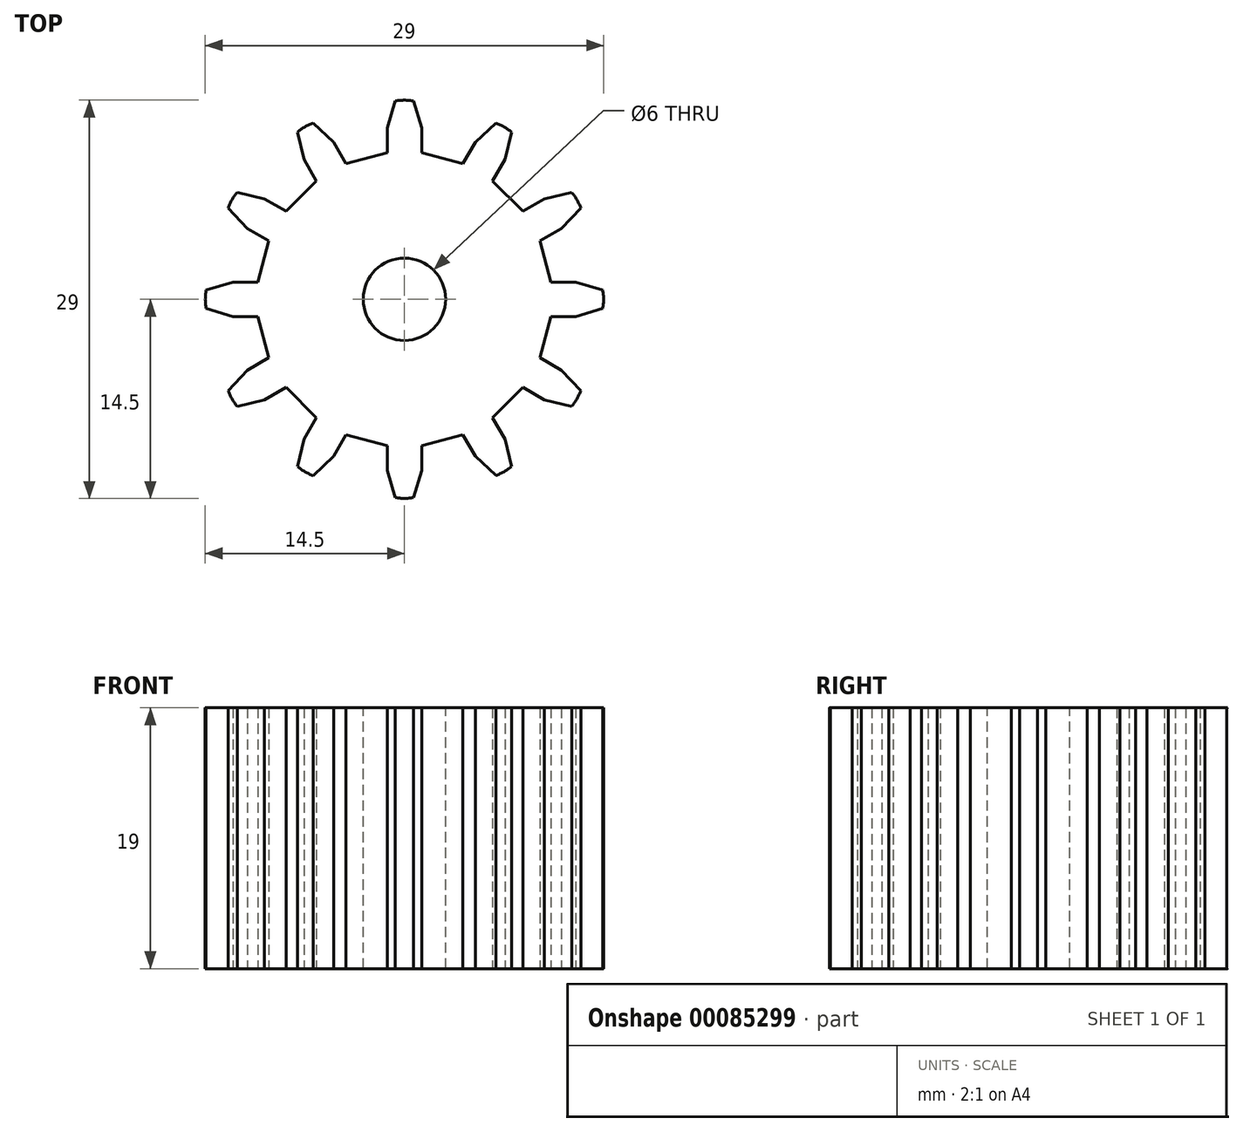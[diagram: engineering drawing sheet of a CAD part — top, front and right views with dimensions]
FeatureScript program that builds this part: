
annotation { "Feature Type Name" : "Feature", "Feature Type Description" : "" }
export const myFeature = defineFeature(function(context is Context, id is Id, definition is map)
    precondition{}
    {
        {
            var Q0;
            Q0=qCreatedBy(makeId("Top.planeOp"),FACE);
            var sketch = newSketch(context, id + "F0", { "sketchPlane" : qUnion([Q0])});
            skCircle(sketch, "E0", {"center": v(0, 0) * mm, "radius": 14.5 * mm});
            skArc(sketch, "E1", {"start": v(-1.25, 10.68) * mm, "mid": v(0, -10.75) * mm, "end": v(1.25, 10.68) * mm});
            skLineSegment(sketch, "E2", {"start": v(0, 10.75) * mm, "end": v(0, 14.5) * mm});
            skLineSegment(sketch, "E3.0", {"start": v(1.25, 10.68) * mm, "end": v(1.25, 14.29) * mm});
            skLineSegment(sketch, "E4.0", {"start": v(-1.25, 10.68) * mm, "end": v(-1.25, 14.29) * mm});
            skArc(sketch, "E5.trimOffspring", {"start": v(1.25, 14.29) * mm, "mid": v(0, 14.5) * mm, "end": v(-1.25, 14.29) * mm});
            skLineSegment(sketch, "E6", {"start": v(-1.25, 14.29) * mm, "end": v(-1.25, 14.45) * mm});
            skLineSegment(sketch, "E7.1.0", {"start": v(-4.26, 9.87) * mm, "end": v(-6.06, 13) * mm});
            skArc(sketch, "E7.1.1", {"start": v(-6.06, 13) * mm, "mid": v(-7.25, 12.56) * mm, "end": v(-8.23, 11.75) * mm});
            skLineSegment(sketch, "E7.1.2", {"start": v(-6.42, 8.62) * mm, "end": v(-8.23, 11.75) * mm});
            skLineSegment(sketch, "E7.2.0", {"start": v(-8.62, 6.42) * mm, "end": v(-11.75, 8.23) * mm});
            skArc(sketch, "E7.2.1", {"start": v(-11.75, 8.23) * mm, "mid": v(-12.56, 7.25) * mm, "end": v(-13, 6.06) * mm});
            skLineSegment(sketch, "E7.2.2", {"start": v(-9.87, 4.26) * mm, "end": v(-13, 6.06) * mm});
            skLineSegment(sketch, "E7.3.0", {"start": v(-10.68, 1.25) * mm, "end": v(-14.29, 1.25) * mm});
            skArc(sketch, "E7.3.1", {"start": v(-14.29, 1.25) * mm, "mid": v(-14.5, 0) * mm, "end": v(-14.29, -1.25) * mm});
            skLineSegment(sketch, "E7.3.2", {"start": v(-10.68, -1.25) * mm, "end": v(-14.29, -1.25) * mm});
            skLineSegment(sketch, "E7.4.0", {"start": v(-9.87, -4.26) * mm, "end": v(-13, -6.06) * mm});
            skArc(sketch, "E7.4.1", {"start": v(-13, -6.06) * mm, "mid": v(-12.56, -7.25) * mm, "end": v(-11.75, -8.23) * mm});
            skLineSegment(sketch, "E7.4.2", {"start": v(-8.62, -6.42) * mm, "end": v(-11.75, -8.23) * mm});
            skLineSegment(sketch, "E7.5.0", {"start": v(-6.42, -8.62) * mm, "end": v(-8.23, -11.75) * mm});
            skArc(sketch, "E7.5.1", {"start": v(-8.23, -11.75) * mm, "mid": v(-7.25, -12.56) * mm, "end": v(-6.06, -13) * mm});
            skLineSegment(sketch, "E7.5.2", {"start": v(-4.26, -9.87) * mm, "end": v(-6.06, -13) * mm});
            skLineSegment(sketch, "E7.6.0", {"start": v(-1.25, -10.68) * mm, "end": v(-1.25, -14.29) * mm});
            skArc(sketch, "E7.6.1", {"start": v(-1.25, -14.29) * mm, "mid": v(0, -14.5) * mm, "end": v(1.25, -14.29) * mm});
            skLineSegment(sketch, "E7.6.2", {"start": v(1.25, -10.68) * mm, "end": v(1.25, -14.29) * mm});
            skLineSegment(sketch, "E7.7.0", {"start": v(4.26, -9.87) * mm, "end": v(6.06, -13) * mm});
            skArc(sketch, "E7.7.1", {"start": v(6.06, -13) * mm, "mid": v(7.25, -12.56) * mm, "end": v(8.23, -11.75) * mm});
            skLineSegment(sketch, "E7.7.2", {"start": v(6.42, -8.62) * mm, "end": v(8.23, -11.75) * mm});
            skLineSegment(sketch, "E7.8.0", {"start": v(8.62, -6.42) * mm, "end": v(11.75, -8.23) * mm});
            skArc(sketch, "E7.8.1", {"start": v(11.75, -8.23) * mm, "mid": v(12.56, -7.25) * mm, "end": v(13, -6.06) * mm});
            skLineSegment(sketch, "E7.8.2", {"start": v(9.87, -4.26) * mm, "end": v(13, -6.06) * mm});
            skLineSegment(sketch, "E7.9.0", {"start": v(10.68, -1.25) * mm, "end": v(14.29, -1.25) * mm});
            skArc(sketch, "E7.9.1", {"start": v(14.29, -1.25) * mm, "mid": v(14.5, 0) * mm, "end": v(14.29, 1.25) * mm});
            skLineSegment(sketch, "E7.9.2", {"start": v(10.68, 1.25) * mm, "end": v(14.29, 1.25) * mm});
            skLineSegment(sketch, "E7.10.0", {"start": v(9.87, 4.26) * mm, "end": v(13, 6.06) * mm});
            skArc(sketch, "E7.10.1", {"start": v(13, 6.06) * mm, "mid": v(12.56, 7.25) * mm, "end": v(11.75, 8.23) * mm});
            skLineSegment(sketch, "E7.10.2", {"start": v(8.62, 6.42) * mm, "end": v(11.75, 8.23) * mm});
            skLineSegment(sketch, "E7.11.0", {"start": v(6.42, 8.62) * mm, "end": v(8.23, 11.75) * mm});
            skArc(sketch, "E7.11.1", {"start": v(8.23, 11.75) * mm, "mid": v(7.25, 12.56) * mm, "end": v(6.06, 13) * mm});
            skLineSegment(sketch, "E7.11.2", {"start": v(4.26, 9.87) * mm, "end": v(6.06, 13) * mm});
            skLineSegment(sketch, "E8", {"start": v(-1.25, 14.45) * mm, "end": v(-0.66, 14.45) * mm});
            skLineSegment(sketch, "E9", {"start": v(-0.66, 14.45) * mm, "end": v(-1.25, 12.48) * mm});
            skLineSegment(sketch, "E10.MirrorCS", {"start": v(0.66, 14.45) * mm, "end": v(1.25, 12.48) * mm});
            skLineSegment(sketch, "E11.1.0", {"start": v(-7.8, 12.18) * mm, "end": v(-7.32, 10.18) * mm});
            skLineSegment(sketch, "E11.1.1", {"start": v(-6.65, 12.84) * mm, "end": v(-5.16, 11.43) * mm});
            skLineSegment(sketch, "E11.2.0", {"start": v(-12.84, 6.65) * mm, "end": v(-11.43, 5.16) * mm});
            skLineSegment(sketch, "E11.2.1", {"start": v(-12.18, 7.8) * mm, "end": v(-10.18, 7.32) * mm});
            skLineSegment(sketch, "E11.3.0", {"start": v(-14.45, -0.66) * mm, "end": v(-12.48, -1.25) * mm});
            skLineSegment(sketch, "E11.3.1", {"start": v(-14.45, 0.66) * mm, "end": v(-12.48, 1.25) * mm});
            skLineSegment(sketch, "E11.4.0", {"start": v(-12.18, -7.8) * mm, "end": v(-10.18, -7.32) * mm});
            skLineSegment(sketch, "E11.4.1", {"start": v(-12.84, -6.65) * mm, "end": v(-11.43, -5.16) * mm});
            skLineSegment(sketch, "E11.5.0", {"start": v(-6.65, -12.84) * mm, "end": v(-5.16, -11.43) * mm});
            skLineSegment(sketch, "E11.5.1", {"start": v(-7.8, -12.18) * mm, "end": v(-7.32, -10.18) * mm});
            skLineSegment(sketch, "E11.6.0", {"start": v(0.66, -14.45) * mm, "end": v(1.25, -12.48) * mm});
            skLineSegment(sketch, "E11.6.1", {"start": v(-0.66, -14.45) * mm, "end": v(-1.25, -12.48) * mm});
            skLineSegment(sketch, "E11.7.0", {"start": v(7.8, -12.18) * mm, "end": v(7.32, -10.18) * mm});
            skLineSegment(sketch, "E11.7.1", {"start": v(6.65, -12.84) * mm, "end": v(5.16, -11.43) * mm});
            skLineSegment(sketch, "E11.8.0", {"start": v(12.84, -6.65) * mm, "end": v(11.43, -5.16) * mm});
            skLineSegment(sketch, "E11.8.1", {"start": v(12.18, -7.8) * mm, "end": v(10.18, -7.32) * mm});
            skLineSegment(sketch, "E11.9.0", {"start": v(14.45, 0.66) * mm, "end": v(12.48, 1.25) * mm});
            skLineSegment(sketch, "E11.9.1", {"start": v(14.45, -0.66) * mm, "end": v(12.48, -1.25) * mm});
            skLineSegment(sketch, "E11.10.0", {"start": v(12.18, 7.8) * mm, "end": v(10.18, 7.32) * mm});
            skLineSegment(sketch, "E11.10.1", {"start": v(12.84, 6.65) * mm, "end": v(11.43, 5.16) * mm});
            skLineSegment(sketch, "E11.11.0", {"start": v(6.65, 12.84) * mm, "end": v(5.16, 11.43) * mm});
            skLineSegment(sketch, "E11.11.1", {"start": v(7.8, 12.18) * mm, "end": v(7.32, 10.18) * mm});
            skSolve(sketch);
        }
        {
            var Q0;
            {var subQ0=sQuery(id+"F0.wireOp",EDGE,"E1");var subQ22=sQuery(id+"F0.wireOp",EDGE,"E4.0");var subQ23=makeQuery(id+"F0.imprint","INTERSECT",VERTEX,{"derivedFrom":[subQ0,subQ22]});Q0=makeQuery(id+"F0.imprint","IMPRINT",FACE,{"disambiguationData":[TD([[makeQuery(id+"F0.imprint","IMPRINT",EDGE,{"disambiguationData":[TD([[subQ23,-1.0]])],"derivedFrom":subQ0}),1.0]])]});}
            var Q1;
            {var subQ6=sQuery(id+"F0.wireOp",EDGE,"E7.1.0");var subQ7=sQuery(id+"F0.wireOp",EDGE,"E1");var subQ8=makeQuery(id+"F0.imprint","INTERSECT",VERTEX,{"derivedFrom":[subQ7,subQ6]});Q1=makeQuery(id+"F0.imprint","IMPRINT",FACE,{"disambiguationData":[TD([[makeQuery(id+"F0.imprint","IMPRINT",EDGE,{"disambiguationData":[TD([[subQ8,-1.0]])],"derivedFrom":subQ7}),-1.0]])]});}
            var Q2;
            {var subQ6=sQuery(id+"F0.wireOp",EDGE,"E7.2.0");var subQ7=sQuery(id+"F0.wireOp",EDGE,"E1");var subQ8=makeQuery(id+"F0.imprint","INTERSECT",VERTEX,{"derivedFrom":[subQ7,subQ6]});Q2=makeQuery(id+"F0.imprint","IMPRINT",FACE,{"disambiguationData":[TD([[makeQuery(id+"F0.imprint","IMPRINT",EDGE,{"disambiguationData":[TD([[subQ8,-1.0]])],"derivedFrom":subQ7}),-1.0]])]});}
            var Q3;
            {var subQ8=sQuery(id+"F0.wireOp",EDGE,"E7.3.0");var subQ9=sQuery(id+"F0.wireOp",EDGE,"E1");var subQ10=makeQuery(id+"F0.imprint","INTERSECT",VERTEX,{"derivedFrom":[subQ9,subQ8]});Q3=makeQuery(id+"F0.imprint","IMPRINT",FACE,{"disambiguationData":[TD([[makeQuery(id+"F0.imprint","IMPRINT",EDGE,{"disambiguationData":[TD([[subQ10,-1.0]])],"derivedFrom":subQ9}),-1.0]])]});}
            var Q4;
            {var subQ6=sQuery(id+"F0.wireOp",EDGE,"E7.11.0");var subQ7=sQuery(id+"F0.wireOp",EDGE,"E1");var subQ8=makeQuery(id+"F0.imprint","INTERSECT",VERTEX,{"derivedFrom":[subQ7,subQ6]});Q4=makeQuery(id+"F0.imprint","IMPRINT",FACE,{"disambiguationData":[TD([[makeQuery(id+"F0.imprint","IMPRINT",EDGE,{"disambiguationData":[TD([[subQ8,-1.0]])],"derivedFrom":subQ7}),-1.0]])]});}
            var Q5;
            {var subQ4=sQuery(id+"F0.wireOp",EDGE,"E7.10.0");var subQ5=sQuery(id+"F0.wireOp",EDGE,"E1");var subQ6=makeQuery(id+"F0.imprint","INTERSECT",VERTEX,{"derivedFrom":[subQ5,subQ4]});Q5=makeQuery(id+"F0.imprint","IMPRINT",FACE,{"disambiguationData":[TD([[makeQuery(id+"F0.imprint","IMPRINT",EDGE,{"disambiguationData":[TD([[subQ6,-1.0]])],"derivedFrom":subQ5}),-1.0]])]});}
            var Q6;
            {var subQ6=sQuery(id+"F0.wireOp",EDGE,"E7.9.0");var subQ7=sQuery(id+"F0.wireOp",EDGE,"E1");var subQ8=makeQuery(id+"F0.imprint","INTERSECT",VERTEX,{"derivedFrom":[subQ7,subQ6]});Q6=makeQuery(id+"F0.imprint","IMPRINT",FACE,{"disambiguationData":[TD([[makeQuery(id+"F0.imprint","IMPRINT",EDGE,{"disambiguationData":[TD([[subQ8,-1.0]])],"derivedFrom":subQ7}),-1.0]])]});}
            var Q7;
            {var subQ6=sQuery(id+"F0.wireOp",EDGE,"E7.6.0");var subQ7=sQuery(id+"F0.wireOp",EDGE,"E1");var subQ8=makeQuery(id+"F0.imprint","INTERSECT",VERTEX,{"derivedFrom":[subQ7,subQ6]});Q7=makeQuery(id+"F0.imprint","IMPRINT",FACE,{"disambiguationData":[TD([[makeQuery(id+"F0.imprint","IMPRINT",EDGE,{"disambiguationData":[TD([[subQ8,-1.0]])],"derivedFrom":subQ7}),-1.0]])]});}
            var Q8;
            {var subQ0=sQuery(id+"F0.wireOp",EDGE,"E7.5.0");var subQ1=sQuery(id+"F0.wireOp",EDGE,"E1");var subQ2=makeQuery(id+"F0.imprint","INTERSECT",VERTEX,{"derivedFrom":[subQ1,subQ0]});Q8=makeQuery(id+"F0.imprint","IMPRINT",FACE,{"disambiguationData":[TD([[makeQuery(id+"F0.imprint","IMPRINT",EDGE,{"disambiguationData":[TD([[subQ2,-1.0]])],"derivedFrom":subQ1}),-1.0]])]});}
            var Q9;
            {var subQ6=sQuery(id+"F0.wireOp",EDGE,"E7.4.0");var subQ7=sQuery(id+"F0.wireOp",EDGE,"E1");var subQ8=makeQuery(id+"F0.imprint","INTERSECT",VERTEX,{"derivedFrom":[subQ7,subQ6]});Q9=makeQuery(id+"F0.imprint","IMPRINT",FACE,{"disambiguationData":[TD([[makeQuery(id+"F0.imprint","IMPRINT",EDGE,{"disambiguationData":[TD([[subQ8,-1.0]])],"derivedFrom":subQ7}),-1.0]])]});}
            var Q10;
            {var subQ4=sQuery(id+"F0.wireOp",EDGE,"E7.8.0");var subQ5=sQuery(id+"F0.wireOp",EDGE,"E1");var subQ6=makeQuery(id+"F0.imprint","INTERSECT",VERTEX,{"derivedFrom":[subQ5,subQ4]});Q10=makeQuery(id+"F0.imprint","IMPRINT",FACE,{"disambiguationData":[TD([[makeQuery(id+"F0.imprint","IMPRINT",EDGE,{"disambiguationData":[TD([[subQ6,-1.0]])],"derivedFrom":subQ5}),-1.0]])]});}
            var Q11;
            {var subQ6=sQuery(id+"F0.wireOp",EDGE,"E7.7.0");var subQ7=sQuery(id+"F0.wireOp",EDGE,"E1");var subQ8=makeQuery(id+"F0.imprint","INTERSECT",VERTEX,{"derivedFrom":[subQ7,subQ6]});Q11=makeQuery(id+"F0.imprint","IMPRINT",FACE,{"disambiguationData":[TD([[makeQuery(id+"F0.imprint","IMPRINT",EDGE,{"disambiguationData":[TD([[subQ8,-1.0]])],"derivedFrom":subQ7}),-1.0]])]});}
            extrude(context, id + "F1", {"entities" : qUnion([Q0, Q1, Q2, Q3, Q4, Q5, Q6, Q7, Q8, Q9, Q10, Q11]), "depth" : 19 * mm});
        }
        {
            var Q0;
            Q0=makeQuery(id+"F1.opExtrude","CAP_FACE",FACE,{"disambiguationData":[OSD([sQuery(id+"F0.wireOp",EDGE,"E1"),sQuery(id+"F0.wireOp",EDGE,"E3.0"),sQuery(id+"F0.wireOp",EDGE,"E4.0"),sQuery(id+"F0.wireOp",EDGE,"E5.trimOffspring"),sQuery(id+"F0.wireOp",EDGE,"E7.1.0"),sQuery(id+"F0.wireOp",EDGE,"E7.1.1"),sQuery(id+"F0.wireOp",EDGE,"E7.1.2"),sQuery(id+"F0.wireOp",EDGE,"E7.2.0"),sQuery(id+"F0.wireOp",EDGE,"E7.2.1"),sQuery(id+"F0.wireOp",EDGE,"E7.2.2"),sQuery(id+"F0.wireOp",EDGE,"E7.3.0"),sQuery(id+"F0.wireOp",EDGE,"E7.3.1"),sQuery(id+"F0.wireOp",EDGE,"E7.3.2"),sQuery(id+"F0.wireOp",EDGE,"E7.4.0"),sQuery(id+"F0.wireOp",EDGE,"E7.4.1"),sQuery(id+"F0.wireOp",EDGE,"E7.4.2"),sQuery(id+"F0.wireOp",EDGE,"E7.5.0"),sQuery(id+"F0.wireOp",EDGE,"E7.5.1"),sQuery(id+"F0.wireOp",EDGE,"E7.5.2"),sQuery(id+"F0.wireOp",EDGE,"E7.6.0"),sQuery(id+"F0.wireOp",EDGE,"E7.6.1"),sQuery(id+"F0.wireOp",EDGE,"E7.6.2"),sQuery(id+"F0.wireOp",EDGE,"E7.7.0"),sQuery(id+"F0.wireOp",EDGE,"E7.7.1"),sQuery(id+"F0.wireOp",EDGE,"E7.7.2"),sQuery(id+"F0.wireOp",EDGE,"E7.8.0"),sQuery(id+"F0.wireOp",EDGE,"E7.8.1"),sQuery(id+"F0.wireOp",EDGE,"E7.8.2"),sQuery(id+"F0.wireOp",EDGE,"E7.9.0"),sQuery(id+"F0.wireOp",EDGE,"E7.9.1"),sQuery(id+"F0.wireOp",EDGE,"E7.9.2"),sQuery(id+"F0.wireOp",EDGE,"E7.10.0"),sQuery(id+"F0.wireOp",EDGE,"E7.10.1"),sQuery(id+"F0.wireOp",EDGE,"E7.10.2"),sQuery(id+"F0.wireOp",EDGE,"E7.11.0"),sQuery(id+"F0.wireOp",EDGE,"E7.11.1"),sQuery(id+"F0.wireOp",EDGE,"E7.11.2")])],"isStart":false});
            var sketch = newSketch(context, id + "F2", { "sketchPlane" : qUnion([Q0])});
            skCircle(sketch, "E12", {"center": v(0, 0) * mm, "radius": 3 * mm});
            skSolve(sketch);
        }
        {
            var Q0;
            Q0=qSketchRegion(id+"F2",true);
            extrude(context, id + "F3", {"entities" : qUnion([Q0]), "operationType" : NewBodyOperationType.REMOVE, "endBound" : BoundingType.THROUGH_ALL, "oppositeDirection" : true, "depth" : 25 * mm});
        }
        {
            var Q0;
            Q0=makeQuery(id+"F1.opExtrude","CAP_FACE",FACE,{"disambiguationData":[OSD([sQuery(id+"F0.wireOp",EDGE,"E1"),sQuery(id+"F0.wireOp",EDGE,"E3.0"),sQuery(id+"F0.wireOp",EDGE,"E4.0"),sQuery(id+"F0.wireOp",EDGE,"E5.trimOffspring"),sQuery(id+"F0.wireOp",EDGE,"E7.1.0"),sQuery(id+"F0.wireOp",EDGE,"E7.1.1"),sQuery(id+"F0.wireOp",EDGE,"E7.1.2"),sQuery(id+"F0.wireOp",EDGE,"E7.2.0"),sQuery(id+"F0.wireOp",EDGE,"E7.2.1"),sQuery(id+"F0.wireOp",EDGE,"E7.2.2"),sQuery(id+"F0.wireOp",EDGE,"E7.3.0"),sQuery(id+"F0.wireOp",EDGE,"E7.3.1"),sQuery(id+"F0.wireOp",EDGE,"E7.3.2"),sQuery(id+"F0.wireOp",EDGE,"E7.4.0"),sQuery(id+"F0.wireOp",EDGE,"E7.4.1"),sQuery(id+"F0.wireOp",EDGE,"E7.4.2"),sQuery(id+"F0.wireOp",EDGE,"E7.5.0"),sQuery(id+"F0.wireOp",EDGE,"E7.5.1"),sQuery(id+"F0.wireOp",EDGE,"E7.5.2"),sQuery(id+"F0.wireOp",EDGE,"E7.6.0"),sQuery(id+"F0.wireOp",EDGE,"E7.6.1"),sQuery(id+"F0.wireOp",EDGE,"E7.6.2"),sQuery(id+"F0.wireOp",EDGE,"E7.7.0"),sQuery(id+"F0.wireOp",EDGE,"E7.7.1"),sQuery(id+"F0.wireOp",EDGE,"E7.7.2"),sQuery(id+"F0.wireOp",EDGE,"E7.8.0"),sQuery(id+"F0.wireOp",EDGE,"E7.8.1"),sQuery(id+"F0.wireOp",EDGE,"E7.8.2"),sQuery(id+"F0.wireOp",EDGE,"E7.9.0"),sQuery(id+"F0.wireOp",EDGE,"E7.9.1"),sQuery(id+"F0.wireOp",EDGE,"E7.9.2"),sQuery(id+"F0.wireOp",EDGE,"E7.10.0"),sQuery(id+"F0.wireOp",EDGE,"E7.10.1"),sQuery(id+"F0.wireOp",EDGE,"E7.10.2"),sQuery(id+"F0.wireOp",EDGE,"E7.11.0"),sQuery(id+"F0.wireOp",EDGE,"E7.11.1"),sQuery(id+"F0.wireOp",EDGE,"E7.11.2")])],"isStart":false});
            var sketch = newSketch(context, id + "F4", { "sketchPlane" : qUnion([Q0])});
            skLineSegment(sketch, "E13", {"start": v(1.25, 10.68) * mm, "end": v(4.26, 9.87) * mm});
            skLineSegment(sketch, "E14", {"start": v(4.26, 9.87) * mm, "end": v(6.42, 8.62) * mm});
            skLineSegment(sketch, "E15", {"start": v(6.42, 8.62) * mm, "end": v(8.62, 6.42) * mm});
            skLineSegment(sketch, "E16", {"start": v(8.62, 6.42) * mm, "end": v(9.87, 4.26) * mm});
            skLineSegment(sketch, "E17", {"start": v(9.87, 4.26) * mm, "end": v(10.68, 1.25) * mm});
            skLineSegment(sketch, "E18", {"start": v(10.68, 1.25) * mm, "end": v(10.68, -1.25) * mm});
            skLineSegment(sketch, "E19", {"start": v(10.68, -1.25) * mm, "end": v(9.87, -4.26) * mm});
            skLineSegment(sketch, "E20", {"start": v(9.87, -4.26) * mm, "end": v(8.62, -6.42) * mm});
            skLineSegment(sketch, "E21", {"start": v(8.62, -6.42) * mm, "end": v(6.42, -8.62) * mm});
            skLineSegment(sketch, "E22", {"start": v(6.42, -8.62) * mm, "end": v(4.26, -9.87) * mm});
            skLineSegment(sketch, "E23", {"start": v(4.26, -9.87) * mm, "end": v(1.25, -10.68) * mm});
            skLineSegment(sketch, "E24", {"start": v(1.25, -10.68) * mm, "end": v(-1.25, -10.68) * mm});
            skLineSegment(sketch, "E25", {"start": v(-1.25, -10.68) * mm, "end": v(-4.26, -9.87) * mm});
            skLineSegment(sketch, "E26", {"start": v(-4.26, -9.87) * mm, "end": v(-6.42, -8.62) * mm});
            skLineSegment(sketch, "E27", {"start": v(-6.42, -8.62) * mm, "end": v(-8.62, -6.42) * mm});
            skLineSegment(sketch, "E28", {"start": v(-8.62, -6.42) * mm, "end": v(-9.87, -4.26) * mm});
            skLineSegment(sketch, "E29", {"start": v(-9.87, -4.26) * mm, "end": v(-10.68, -1.25) * mm});
            skLineSegment(sketch, "E30", {"start": v(-10.68, -1.25) * mm, "end": v(-10.68, 1.25) * mm});
            skLineSegment(sketch, "E31", {"start": v(-10.68, 1.25) * mm, "end": v(-9.87, 4.26) * mm});
            skLineSegment(sketch, "E32", {"start": v(-9.87, 4.26) * mm, "end": v(-8.62, 6.42) * mm});
            skLineSegment(sketch, "E33", {"start": v(-8.62, 6.42) * mm, "end": v(-6.42, 8.62) * mm});
            skLineSegment(sketch, "E34", {"start": v(-6.42, 8.62) * mm, "end": v(-4.26, 9.87) * mm});
            skLineSegment(sketch, "E35", {"start": v(-4.26, 9.87) * mm, "end": v(-1.25, 10.68) * mm});
            skLineSegment(sketch, "E36", {"start": v(-1.25, 10.68) * mm, "end": v(1.25, 10.68) * mm});
            skSolve(sketch);
        }
        {
            var Q0;
            Q0=makeQuery(id+"F4.imprint","IMPRINT",FACE,{"disambiguationData":[TD([[makeQuery(id+"F4.imprint","IMPRINT",EDGE,{"derivedFrom":sQuery(id+"F4.wireOp",EDGE,"E31")}),1.0]])]});
            var Q1;
            Q1=makeQuery(id+"F4.imprint","IMPRINT",FACE,{"disambiguationData":[TD([[makeQuery(id+"F4.imprint","IMPRINT",EDGE,{"derivedFrom":sQuery(id+"F4.wireOp",EDGE,"E29")}),1.0]])]});
            var Q2;
            Q2=makeQuery(id+"F4.imprint","IMPRINT",FACE,{"disambiguationData":[TD([[makeQuery(id+"F4.imprint","IMPRINT",EDGE,{"derivedFrom":sQuery(id+"F4.wireOp",EDGE,"E33")}),1.0]])]});
            var Q3;
            Q3=makeQuery(id+"F4.imprint","IMPRINT",FACE,{"disambiguationData":[TD([[makeQuery(id+"F4.imprint","IMPRINT",EDGE,{"derivedFrom":sQuery(id+"F4.wireOp",EDGE,"E35")}),1.0]])]});
            var Q4;
            Q4=makeQuery(id+"F4.imprint","IMPRINT",FACE,{"disambiguationData":[TD([[makeQuery(id+"F4.imprint","IMPRINT",EDGE,{"derivedFrom":sQuery(id+"F4.wireOp",EDGE,"E13")}),1.0]])]});
            var Q5;
            Q5=makeQuery(id+"F4.imprint","IMPRINT",FACE,{"disambiguationData":[TD([[makeQuery(id+"F4.imprint","IMPRINT",EDGE,{"derivedFrom":sQuery(id+"F4.wireOp",EDGE,"E15")}),1.0]])]});
            var Q6;
            Q6=makeQuery(id+"F4.imprint","IMPRINT",FACE,{"disambiguationData":[TD([[makeQuery(id+"F4.imprint","IMPRINT",EDGE,{"derivedFrom":sQuery(id+"F4.wireOp",EDGE,"E17")}),1.0]])]});
            var Q7;
            Q7=makeQuery(id+"F4.imprint","IMPRINT",FACE,{"disambiguationData":[TD([[makeQuery(id+"F4.imprint","IMPRINT",EDGE,{"derivedFrom":sQuery(id+"F4.wireOp",EDGE,"E19")}),1.0]])]});
            var Q8;
            Q8=makeQuery(id+"F4.imprint","IMPRINT",FACE,{"disambiguationData":[TD([[makeQuery(id+"F4.imprint","IMPRINT",EDGE,{"derivedFrom":sQuery(id+"F4.wireOp",EDGE,"E21")}),1.0]])]});
            var Q9;
            Q9=makeQuery(id+"F4.imprint","IMPRINT",FACE,{"disambiguationData":[TD([[makeQuery(id+"F4.imprint","IMPRINT",EDGE,{"derivedFrom":sQuery(id+"F4.wireOp",EDGE,"E23")}),1.0]])]});
            var Q10;
            Q10=makeQuery(id+"F4.imprint","IMPRINT",FACE,{"disambiguationData":[TD([[makeQuery(id+"F4.imprint","IMPRINT",EDGE,{"derivedFrom":sQuery(id+"F4.wireOp",EDGE,"E25")}),1.0]])]});
            var Q11;
            Q11=makeQuery(id+"F4.imprint","IMPRINT",FACE,{"disambiguationData":[TD([[makeQuery(id+"F4.imprint","IMPRINT",EDGE,{"derivedFrom":sQuery(id+"F4.wireOp",EDGE,"E27")}),1.0]])]});
            extrude(context, id + "F5", {"entities" : qUnion([Q0, Q1, Q2, Q3, Q4, Q5, Q6, Q7, Q8, Q9, Q10, Q11]), "operationType" : NewBodyOperationType.REMOVE, "endBound" : BoundingType.THROUGH_ALL, "oppositeDirection" : true, "depth" : 25 * mm});
        }
    });
